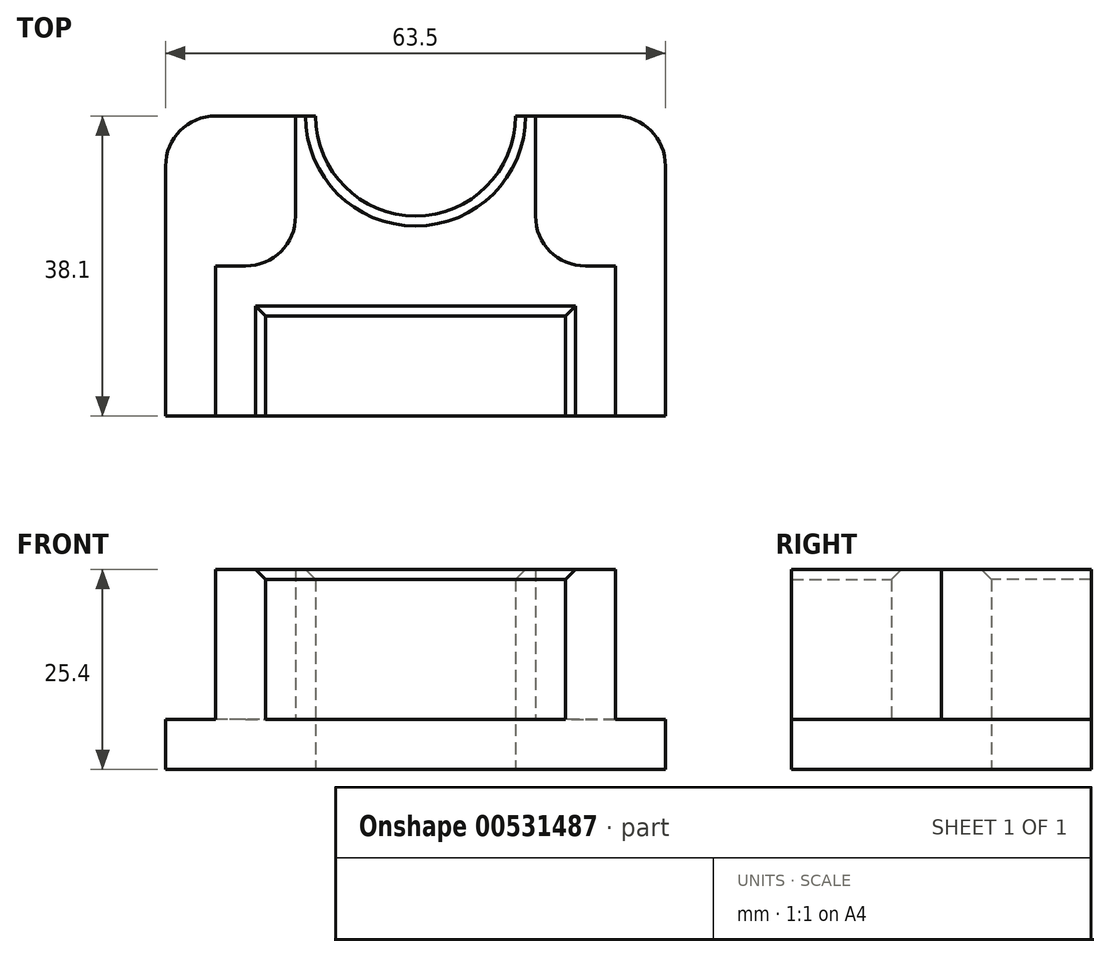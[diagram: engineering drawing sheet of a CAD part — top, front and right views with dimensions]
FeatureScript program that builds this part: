
annotation { "Feature Type Name" : "Feature", "Feature Type Description" : "" }
export const myFeature = defineFeature(function(context is Context, id is Id, definition is map)
    precondition{}
    {
        {
            var Q0;
            Q0=qCreatedBy(makeId("Top.planeOp"),FACE);
            var sketch = newSketch(context, id + "F0", { "sketchPlane" : qUnion([Q0])});
            skLineSegment(sketch, "E0.bottom", {"start": v(31.75, -19.05) * mm, "end": v(-31.75, -19.05) * mm});
            skLineSegment(sketch, "E0.top", {"start": v(25.4, 19.05) * mm, "end": v(12.7, 19.05) * mm});
            skLineSegment(sketch, "E0.left", {"start": v(31.75, -19.05) * mm, "end": v(31.75, 12.7) * mm});
            skLineSegment(sketch, "E0.right", {"start": v(-31.75, -19.05) * mm, "end": v(-31.75, 12.7) * mm});
            skPoint(sketch, "E0.middle", {"position": v(0, 0) * mm});
            skArc(sketch, "E1", {"start": v(-12.7, 19.05) * mm, "mid": v(0, 6.35) * mm, "end": v(12.7, 19.05) * mm});
            skLineSegment(sketch, "E2.trimOffspring", {"start": v(-12.7, 19.05) * mm, "end": v(-25.4, 19.05) * mm});
            skPoint(sketch, "E3.visualSharp", {"position": v(31.75, 19.05) * mm});
            skArc(sketch, "E3.filletArc", {"start": v(31.75, 12.7) * mm, "mid": v(29.9, 17.2) * mm, "end": v(25.4, 19.05) * mm});
            skPoint(sketch, "E4.visualSharp", {"position": v(-31.75, 19.05) * mm});
            skArc(sketch, "E4.filletArc", {"start": v(-25.4, 19.05) * mm, "mid": v(-29.9, 17.2) * mm, "end": v(-31.75, 12.7) * mm});
            skSolve(sketch);
        }
        {
            var Q0;
            Q0=makeQuery(id+"F0.imprint","IMPRINT",FACE,{"disambiguationData":[TD([[makeQuery(id+"F0.imprint","IMPRINT",EDGE,{"derivedFrom":sQuery(id+"F0.wireOp",EDGE,"E0.bottom")}),-1.0]])]});
            extrude(context, id + "F1", {"entities" : qUnion([Q0]), "depth" : 6.35 * mm, "offsetDistance" : 25.4 * mm});
        }
        {
            var Q0;
            Q0=makeQuery(id+"F1.opExtrude","CAP_FACE",FACE,{"disambiguationData":[OSD([sQuery(id+"F0.wireOp",EDGE,"E0.bottom"),sQuery(id+"F0.wireOp",EDGE,"E0.top"),sQuery(id+"F0.wireOp",EDGE,"E0.left"),sQuery(id+"F0.wireOp",EDGE,"E0.right"),sQuery(id+"F0.wireOp",EDGE,"E1"),sQuery(id+"F0.wireOp",EDGE,"E2.trimOffspring"),sQuery(id+"F0.wireOp",EDGE,"E3.filletArc"),sQuery(id+"F0.wireOp",EDGE,"E4.filletArc")])],"isStart":false});
            var sketch = newSketch(context, id + "F2", { "sketchPlane" : qUnion([Q0])});
            skPoint(sketch, "E5.middle", {"position": v(0, -19.05) * mm});
            skLineSegment(sketch, "E6", {"start": v(-25.4, -19.05) * mm, "end": v(-15.24, -19.05) * mm});
            skLineSegment(sketch, "E7", {"start": v(25.4, -19.05) * mm, "end": v(25.4, 0) * mm});
            skLineSegment(sketch, "E8", {"start": v(-25.4, 0) * mm, "end": v(-25.4, -19.05) * mm});
            skLineSegment(sketch, "E9.bottom", {"start": v(19.05, -6.35) * mm, "end": v(-19.05, -6.35) * mm});
            skLineSegment(sketch, "E9.left", {"start": v(19.05, -6.35) * mm, "end": v(19.05, -19.05) * mm});
            skLineSegment(sketch, "E9.right", {"start": v(-19.05, -6.35) * mm, "end": v(-19.05, -19.05) * mm});
            skPoint(sketch, "E9.top.end.orphan", {"position": v(-19.05, -31.75) * mm});
            skPoint(sketch, "E9.top.start.orphan", {"position": v(19.05, -31.75) * mm});
            skLineSegment(sketch, "E10.top", {"start": v(15.24, -19.05) * mm, "end": v(-15.24, -19.05) * mm});
            skPoint(sketch, "E10.middle", {"position": v(0, 0) * mm});
            skLineSegment(sketch, "E11.trimOffspring", {"start": v(0, -19.05) * mm, "end": v(25.4, -19.05) * mm});
            skPoint(sketch, "E12.orphan", {"position": v(-25.4, 19.05) * mm});
            skPoint(sketch, "E13.orphan", {"position": v(25.4, 19.05) * mm});
            skLineSegment(sketch, "E14.trimOffspring", {"start": v(-21.59, 0) * mm, "end": v(-25.4, 0) * mm});
            skPoint(sketch, "E15.visualSharp", {"position": v(-15.24, 0) * mm});
            skArc(sketch, "E15.filletArc", {"start": v(-21.59, 0) * mm, "mid": v(-17.1, 1.86) * mm, "end": v(-15.24, 6.35) * mm});
            skLineSegment(sketch, "E16", {"start": v(21.59, 0) * mm, "end": v(25.4, 0) * mm});
            skPoint(sketch, "E17.visualSharp", {"position": v(15.24, 0) * mm});
            skArc(sketch, "E17.filletArc", {"start": v(15.24, 6.35) * mm, "mid": v(17.1, 1.86) * mm, "end": v(21.59, 0) * mm});
            skLineSegment(sketch, "E18", {"start": v(-15.24, 6.35) * mm, "end": v(-15.24, 19.05) * mm});
            skLineSegment(sketch, "E19", {"start": v(15.24, 6.35) * mm, "end": v(15.24, 19.05) * mm});
            skSolve(sketch);
        }
        {
            var Q0;
            {var subQ1=sQuery(id+"F2.wireOp",EDGE,"E7");Q0=makeQuery(id+"F2.imprint","IMPRINT",FACE,{"disambiguationData":[TD([[makeQuery(id+"F2.imprint","IMPRINT",EDGE,{"derivedFrom":subQ1}),1.0]])]});}
            extrude(context, id + "F3", {"entities" : qUnion([Q0]), "operationType" : NewBodyOperationType.ADD, "depth" : 19.05 * mm, "offsetDistance" : 25.4 * mm});
        }
        {
            var Q0;
            Q0=makeQuery(id+"F3.opExtrude","CAP_EDGE",EDGE,{"disambiguationData":[OSD([sQuery(id+"F0.wireOp",EDGE,"E1")])],"isStart":false});
            var Q1;
            Q1=makeQuery(id+"F3.opExtrude","CAP_EDGE",EDGE,{"disambiguationData":[OSD([sQuery(id+"F2.wireOp",EDGE,"E9.bottom")])],"isStart":false});
            var Q2;
            Q2=makeQuery(id+"F3.opExtrude","CAP_EDGE",EDGE,{"disambiguationData":[OSD([sQuery(id+"F2.wireOp",EDGE,"E9.right")])],"isStart":false});
            var Q3;
            Q3=makeQuery(id+"F3.opExtrude","CAP_EDGE",EDGE,{"disambiguationData":[OSD([sQuery(id+"F2.wireOp",EDGE,"E9.left")])],"isStart":false});
            chamfer(context, id + "F4", {"entities" : qUnion([Q0, Q1, Q2, Q3]), "width" : 1.27 * mm, "tangentPropagation" : true});
        }
    });
